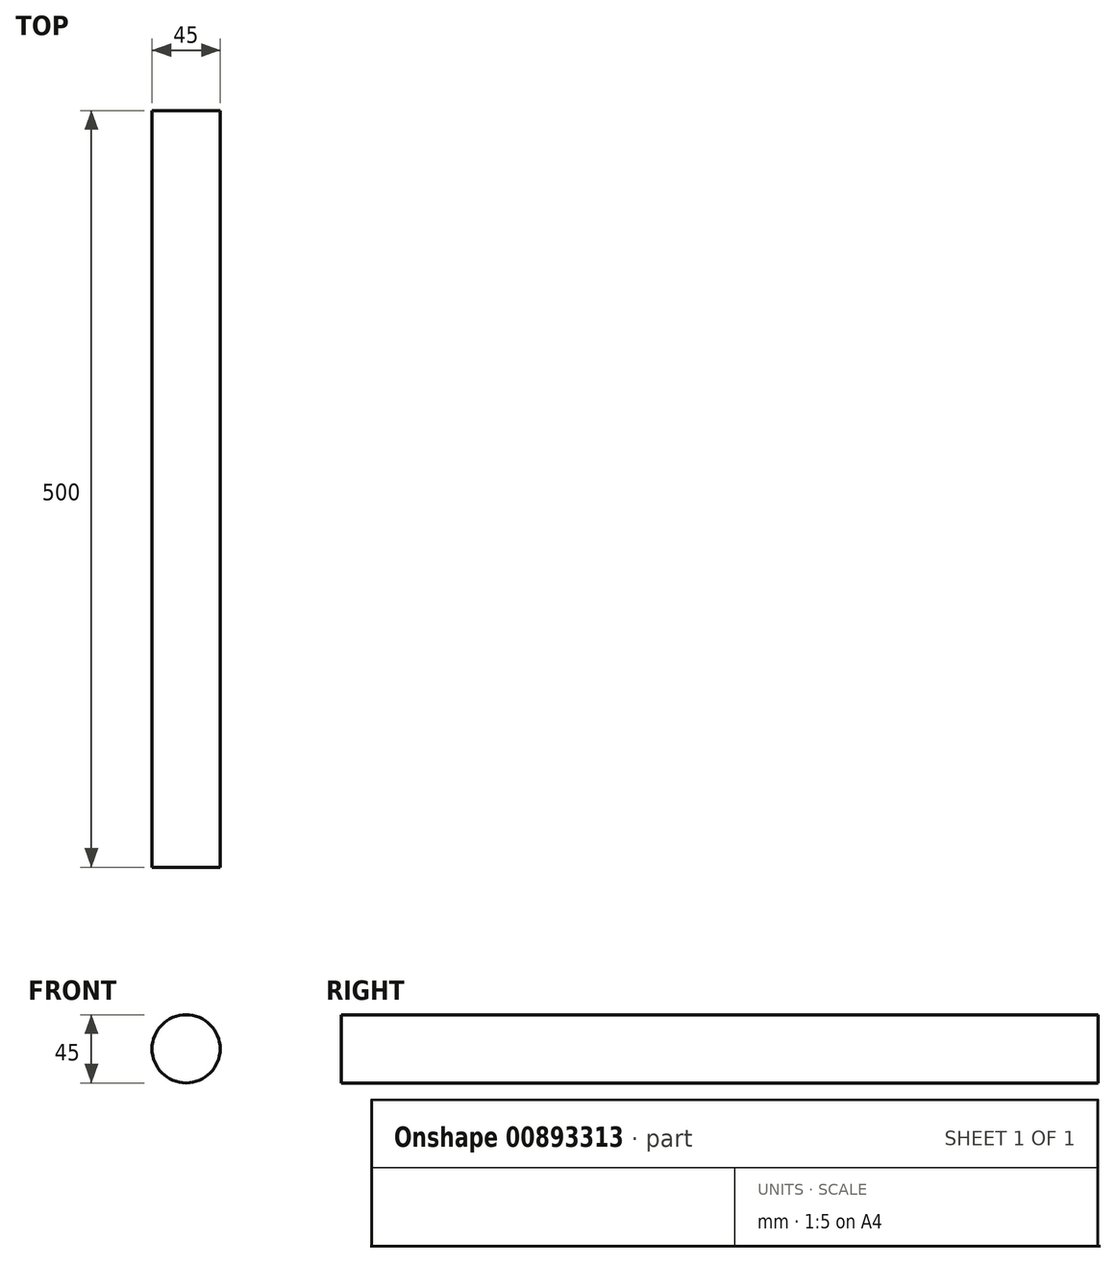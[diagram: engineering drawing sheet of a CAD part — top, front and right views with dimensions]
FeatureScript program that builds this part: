
annotation { "Feature Type Name" : "Feature", "Feature Type Description" : "" }
export const myFeature = defineFeature(function(context is Context, id is Id, definition is map)
    precondition{}
    {
        {
            var Q0;
            Q0=qCreatedBy(makeId("Front.planeOp"),FACE);
            var sketch = newSketch(context, id + "F0", { "sketchPlane" : qUnion([Q0])});
            skCircle(sketch, "E0", {"center": v(0, 0) * mm, "radius": 22.5 * mm});
            skSolve(sketch);
        }
        {
            var Q0;
            Q0=makeQuery(id+"F0.imprint","IMPRINT",FACE,{"disambiguationData":[TD([[makeQuery(id+"F0.imprint","IMPRINT",EDGE,{"derivedFrom":sQuery(id+"F0.wireOp",EDGE,"E0")}),1.0]])]});
            extrude(context, id + "F1", {"entities" : qUnion([Q0]), "depth" : 500 * mm, "offsetDistance" : 25 * mm});
        }
    });
